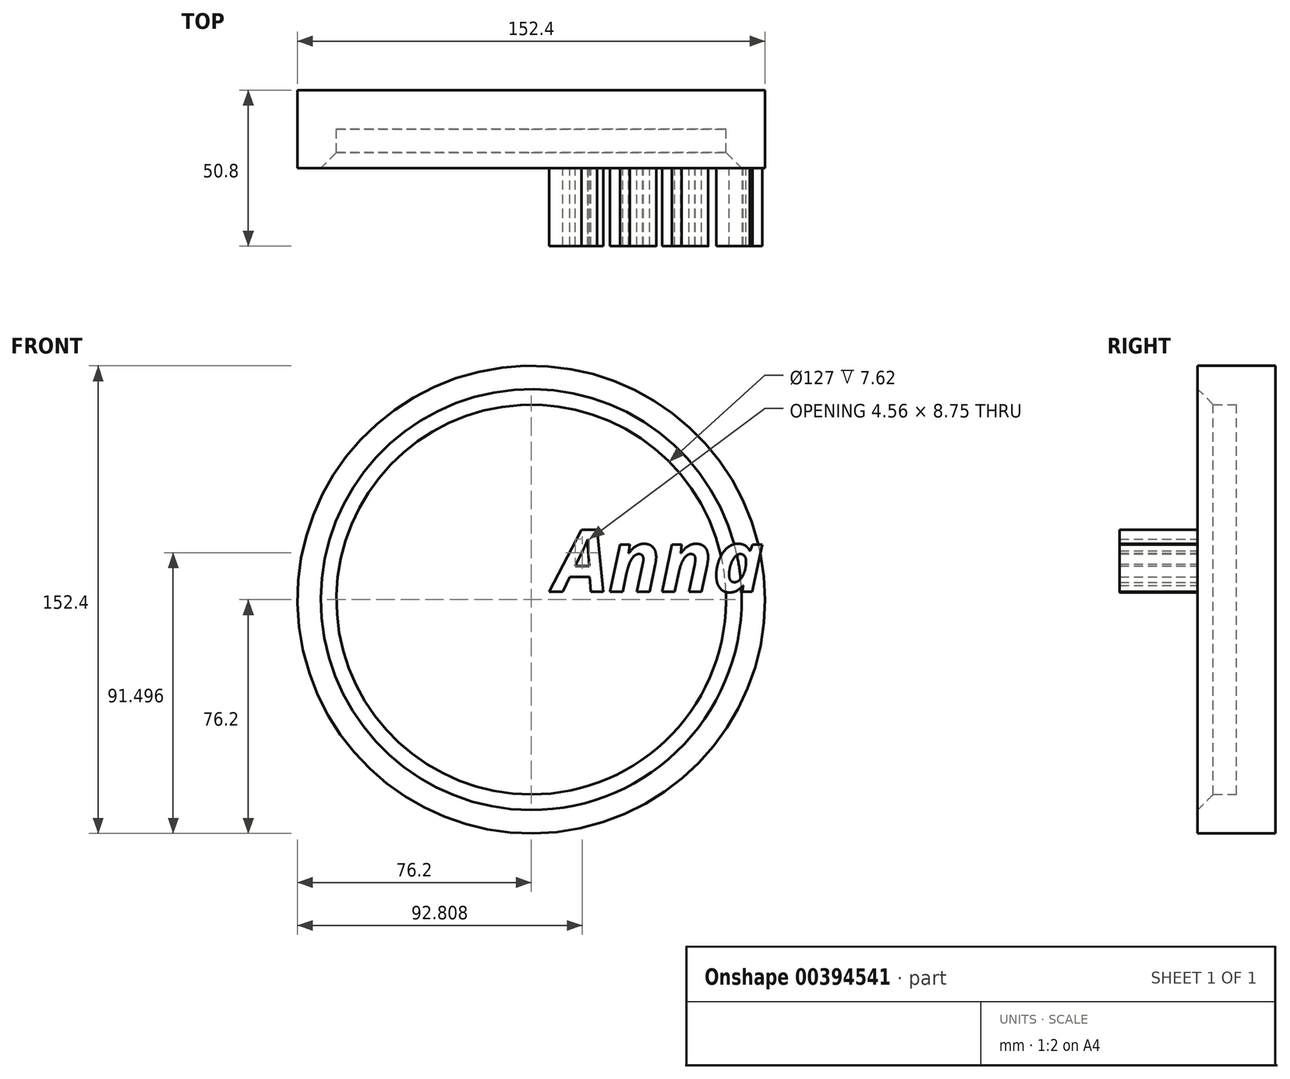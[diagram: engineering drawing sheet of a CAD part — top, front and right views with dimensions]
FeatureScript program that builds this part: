
annotation { "Feature Type Name" : "Feature", "Feature Type Description" : "" }
export const myFeature = defineFeature(function(context is Context, id is Id, definition is map)
    precondition{}
    {
        {
            var Q0;
            Q0=qCreatedBy(makeId("Front.planeOp"),FACE);
            var sketch = newSketch(context, id + "F0", { "sketchPlane" : qUnion([Q0])});
            skCircle(sketch, "E0", {"center": v(0, 0) * mm, "radius": 76.2 * mm});
            skSolve(sketch);
        }
        {
            var Q0;
            Q0 = qSketchRegion(id + "F0", true);
            extrude(context, id + "F1", {"entities" : qUnion([Q0]), "depth" : 25.4 * mm});
        }
        {
            var Q0;
            Q0=makeQuery(id+"F1.opExtrude","CAP_FACE",FACE,{"disambiguationData":[OSD([sQuery(id+"F0.wireOp",EDGE,"E0")])],"isStart":false});
            var sketch = newSketch(context, id + "F2", { "sketchPlane" : qUnion([Q0])});
            skSolve(sketch);
        }
        {
            var Q0;
            Q0=makeQuery(id+"F1.opExtrude","CAP_FACE",FACE,{"disambiguationData":[OSD([sQuery(id+"F0.wireOp",EDGE,"E0")])],"isStart":false});
            shell(context, id + "F3", {"entities" : qUnion([Q0]), "thickness" : 12.7 * mm});
        }
        {
            var Q0;
            {var subQ0=sQuery(id+"F0.wireOp",EDGE,"E0");Q0=makeQuery(id+"F3.opShell","OFFSET_EDGE",EDGE,{"disambiguationData":[OSD([subQ0]),TDD([makeQuery(id+"F1.opExtrude","CAP_EDGE",EDGE,{"disambiguationData":[OSD([subQ0])],"isStart":false})])]});}
            chamfer(context, id + "F4", {"entities" : qUnion([Q0]), "width" : 5.08 * mm, "tangentPropagation" : true});
        }
        {
            var Q0;
            Q0=makeQuery(id+"F2.imprint","IMPRINT",FACE,{"disambiguationData":[TD([[makeQuery(id+"F2.imprint","IMPRINT",EDGE,{"derivedFrom":makeQuery(id+"F1.opExtrude","CAP_EDGE",EDGE,{"disambiguationData":[OSD([sQuery(id+"F0.wireOp",EDGE,"E0")])],"isStart":false})}),1.0]])]});
            var sketch = newSketch(context, id + "F5", { "sketchPlane" : qUnion([Q0])});
            skText(sketch, "E1", { "text": "Anna", "fontName": "OpenSans-BoldItalic.ttf"});
            const initialGuessF5  = {"E1": [0.00756, 0.00259, 1, 0, 0.0202]};
            skSetInitialGuess(sketch, initialGuessF5);
            skSolve(sketch);
        }
        {
            var Q0;
            Q0 = qSketchRegion(id + "F5", true);
            extrude(context, id + "F6", {"entities" : qUnion([Q0]), "operationType" : NewBodyOperationType.ADD, "depth" : 25.4 * mm});
        }
    });
